# Revit family: dimozachitnay_stora_firetechnics_e120_bez_orachenia_vodoi
name_source: partatom
category: Двери
revit_build: Autodesk Revit 2016 (Build: 20160314_0715(x64)
units: mm (PartAtom-declared; Revit-internal decimal feet)

## family parameters
Всегда вертикально = Да
На основе рабочей плоскости = Нет
Общий = Нет
При загрузке вырезать с полостями = Нет
Точка расчета площади = Нет

## types (1)
- Дымозащитная штора E120 (без орошения)
    ADSK_URL страницы изделия = https://www.fire-tec.ru
    ADSK_Наименование = Противопожарная дымозащитная штора E120
    ADSK_Предел огнестойкости = 120 минут
    URL = https://www.fire-tec.ru
    Аналитическая конструкция = <Нет>
    Высота = 0 мм
    Высота грузила = 50 мм
    Высота, макс. = 6.5м
    Изготовитель = Firetechnics
    Материал_ Шторы = Firetex™ 600
    Материал_Короба = Сталь_оцинкованная_листовая Firetechnics
    Примерная высота = 0 мм
    Примерная ширина = 0 мм
    Скорость опускания шторы = 0.15м/c
    Толщина = 0 мм
    Ширина = 0 мм
    Ширина, макс. = 5м

## geometry (parser evidence)
native form markers: Blend x2
no freeform markers — native parametric forms only
